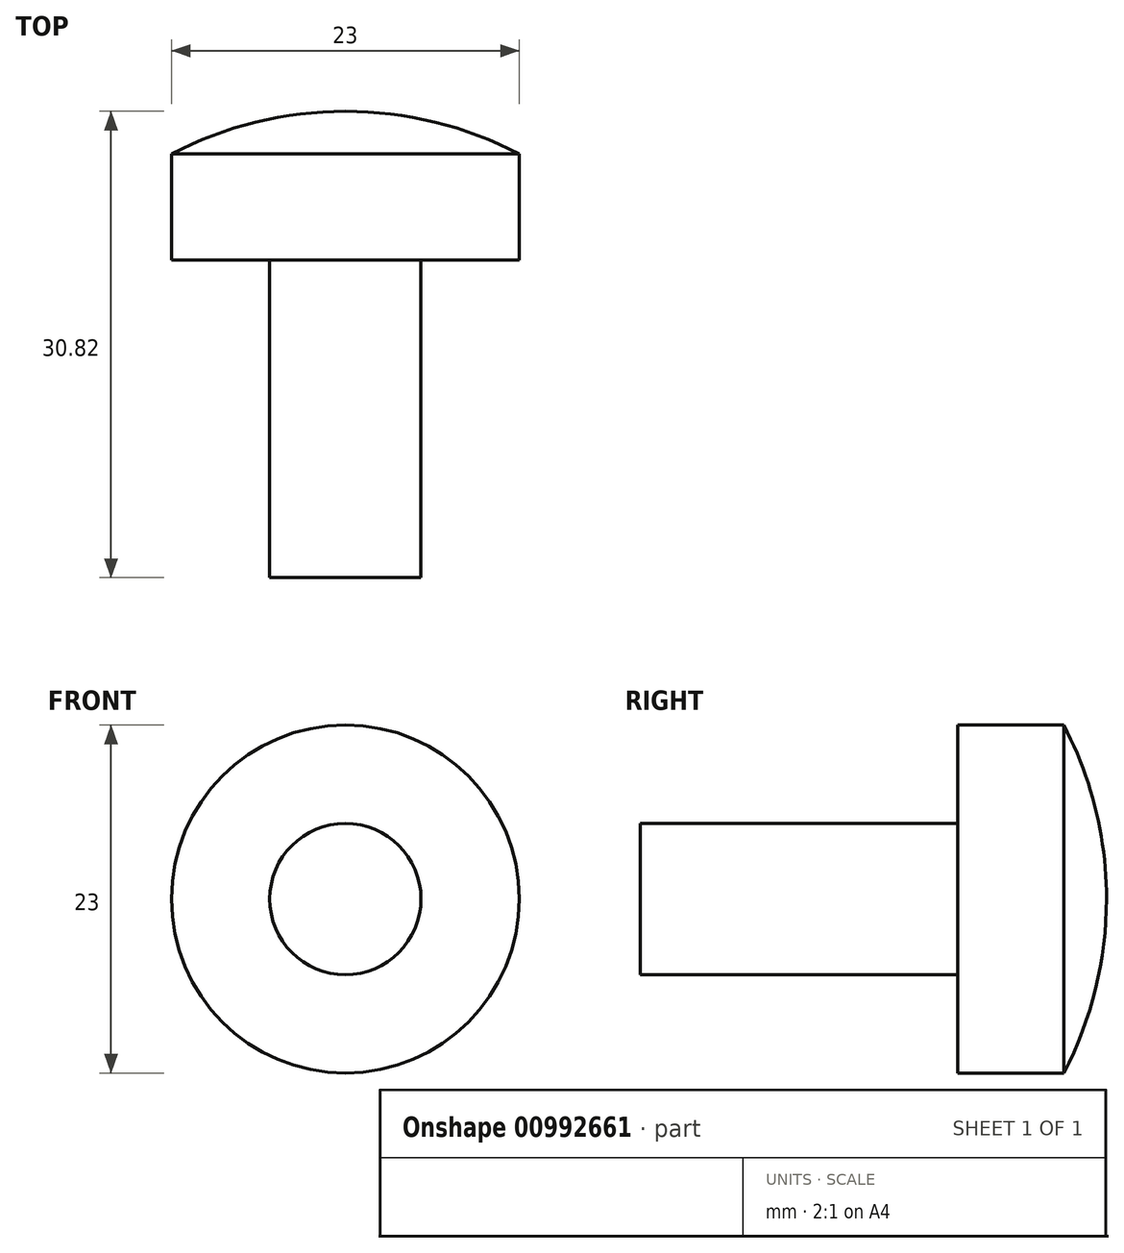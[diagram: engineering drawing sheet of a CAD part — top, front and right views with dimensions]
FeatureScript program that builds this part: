
annotation { "Feature Type Name" : "Feature", "Feature Type Description" : "" }
export const myFeature = defineFeature(function(context is Context, id is Id, definition is map)
    precondition{}
    {
        {
            var Q0;
            Q0=qCreatedBy(makeId("Right.planeOp"),FACE);
            var sketch = newSketch(context, id + "F0", { "sketchPlane" : qUnion([Q0])});
            skLineSegment(sketch, "E0", {"start": v(-30.82, 0) * mm, "end": v(-30.82, 5) * mm});
            skLineSegment(sketch, "E1", {"start": v(-30.82, 5) * mm, "end": v(-9.82, 5) * mm});
            skLineSegment(sketch, "E2", {"start": v(-9.82, 5) * mm, "end": v(-9.82, 11.5) * mm});
            skLineSegment(sketch, "E3", {"start": v(-9.82, 11.5) * mm, "end": v(-2.82, 11.5) * mm});
            skArc(sketch, "E4", {"start": v(0, 0) * mm, "mid": v(-0.72, 5.92) * mm, "end": v(-2.82, 11.5) * mm});
            skLineSegment(sketch, "E5", {"start": v(-30.82, 0) * mm, "end": v(0, 0) * mm});
            skPoint(sketch, "E6.MirrorCS.start.orphan", {"position": v(-30.82, 0) * mm});
            skPoint(sketch, "E7.MirrorCS.start.orphan", {"position": v(0, 0) * mm});
            skLineSegment(sketch, "E8", {"start": v(0, 0) * mm, "end": v(0, 54.03) * mm, "construction": true});
            skLineSegment(sketch, "E9", {"start": v(0, 54.03) * mm, "end": v(0, 54.03) * mm});
            skSolve(sketch);
        }
        {
            var Q0;
            Q0 = qSketchRegion(id + "F0", true);
            var Q1;
            Q1=sQuery(id+"F0.wireOp",EDGE,"E5");
            revolve(context, id + "F1", {"surfaceOperationType" : NewSurfaceOperationType.NEW, "entities" : qUnion([Q0]), "axis" : qUnion([Q1]), "revolveType" : RevolveType.FULL});
        }
    });
